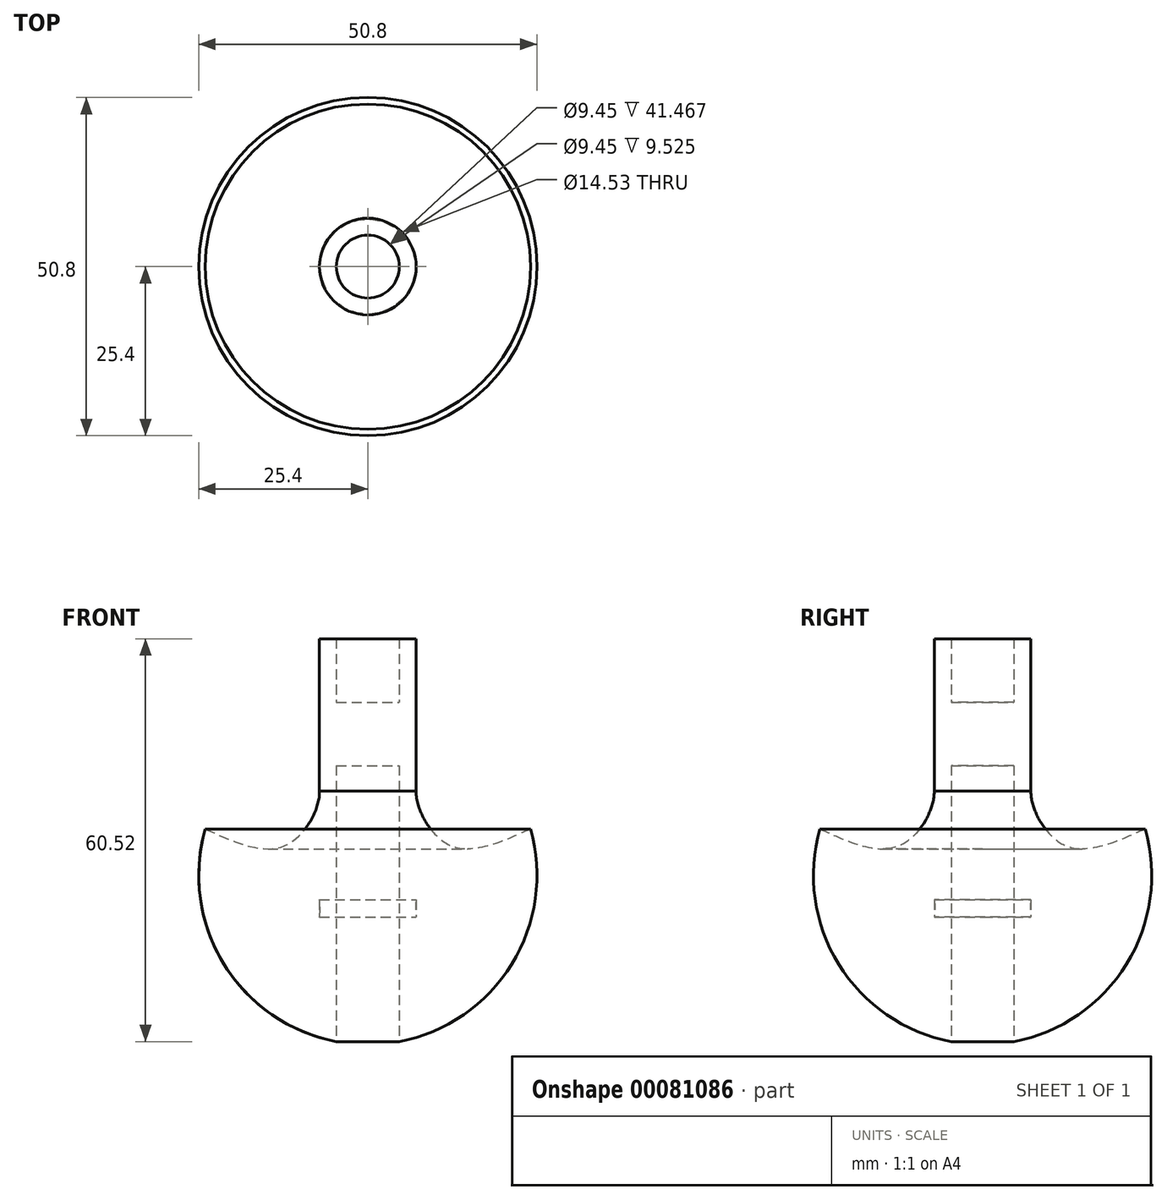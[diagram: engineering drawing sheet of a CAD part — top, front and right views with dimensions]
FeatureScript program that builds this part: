
annotation { "Feature Type Name" : "Feature", "Feature Type Description" : "" }
export const myFeature = defineFeature(function(context is Context, id is Id, definition is map)
    precondition{}
    {
        {
            var Q0;
            Q0=qCreatedBy(makeId("Front.planeOp"),FACE);
            var sketch = newSketch(context, id + "F0", { "sketchPlane" : qUnion([Q0])});
            skArc(sketch, "E0", {"start": v(-22.54, 16.5) * mm, "mid": v(-25.88, -10.52) * mm, "end": v(-4.63, -27.55) * mm});
            skArc(sketch, "E1", {"start": v(-19.3, 16.5) * mm, "mid": v(-23.4, -9.9) * mm, "end": v(-1.6, -25.35) * mm});
            skLineSegment(sketch, "E2", {"start": v(0, 0) * mm, "end": v(0, 16.51) * mm});
            skLineSegment(sketch, "E3", {"start": v(0, 16.51) * mm, "end": v(-7.26, 16.51) * mm});
            skLineSegment(sketch, "E4", {"start": v(-22.54, 16.51) * mm, "end": v(-19.3, 16.51) * mm});
            skLineSegment(sketch, "E5", {"start": v(0, 0) * mm, "end": v(0, -27.94) * mm});
            skLineSegment(sketch, "E6", {"start": v(0, -27.94) * mm, "end": v(0, 35.56) * mm});
            skLineSegment(sketch, "E7", {"start": v(-4.72, 35.56) * mm, "end": v(-4.72, -24.96) * mm});
            skLineSegment(sketch, "E8", {"start": v(-4.72, 35.56) * mm, "end": v(-7.26, 35.56) * mm});
            skLineSegment(sketch, "E9", {"start": v(-7.26, 35.56) * mm, "end": v(-7.26, -24.34) * mm});
            skLineSegment(sketch, "E10", {"start": v(0, 35.56) * mm, "end": v(0, 26.03) * mm});
            skLineSegment(sketch, "E11", {"start": v(0, 26.03) * mm, "end": v(-4.72, 26.03) * mm});
            skLineSegment(sketch, "E12.trimOffspring", {"start": v(-7.26, 16.51) * mm, "end": v(22.54, 16.51) * mm});
            skLineSegment(sketch, "E13.trimOffspring", {"start": v(-19.3, 16.51) * mm, "end": v(-22.54, 16.51) * mm});
            skPoint(sketch, "E14", {"position": v(-15.1, 0) * mm});
            skPoint(sketch, "E15", {"position": v(-7.26, -3.67) * mm});
            skPoint(sketch, "E16", {"position": v(-16.16, -5.93) * mm});
            skPoint(sketch, "E17", {"position": v(-24.25, -7.55) * mm});
            skLineSegment(sketch, "E18", {"start": v(-24.25, -7.55) * mm, "end": v(-24.25, -7.55) * mm});
            skPoint(sketch, "E19", {"position": v(-7.26, 12.37) * mm});
            skPoint(sketch, "E20", {"position": v(-24.43, 6.97) * mm});
            skPoint(sketch, "E21", {"position": v(-12.38, 4.51) * mm});
            skPoint(sketch, "E22.3.internal.snap0", {"position": v(7.64, 16.51) * mm});
            skFitSpline(sketch, "E22", {"points": [v(-24.43, 6.97) * mm, v(-12.38, 4.51) * mm, v(-7.26, 12.37) * mm, v(-9.1, 16.51) * mm], "startDerivative": vector(32.41, -14.69) * mm, "endDerivative": vector(-11.55, 14.27) * mm});
            skArc(sketch, "E23.trimOffspring", {"start": v(-7.26, -6.25) * mm, "mid": v(-7.17, -4.96) * mm, "end": v(-7.26, -3.67) * mm});
            skLineSegment(sketch, "E24", {"start": v(-1.6, -27.8) * mm, "end": v(-13.82, -26.79) * mm});
            skLineSegment(sketch, "E25", {"start": v(0, -27.94) * mm, "end": v(0, -5.84) * mm});
            skLineSegment(sketch, "E26", {"start": v(0, -5.84) * mm, "end": v(-1.6, -5.84) * mm});
            skLineSegment(sketch, "E27", {"start": v(-1.6, -5.84) * mm, "end": v(-1.6, -27.8) * mm});
            skArc(sketch, "E28.trimOffspring", {"start": v(0, -27.94) * mm, "mid": v(24.92, -12.64) * mm, "end": v(22.54, 16.51) * mm});
            skArc(sketch, "E29.trimOffspring", {"start": v(0, -25.4) * mm, "mid": v(23.07, -10.63) * mm, "end": v(19.3, 16.51) * mm});
            skSolve(sketch);
        }
        {
            var Q0;
            {var subQ0=sQuery(id+"F0.wireOp",EDGE,"E18");var subQ1=sQuery(id+"F0.wireOp",EDGE,"E9");var subQ2=makeQuery(id+"F0.imprint","INTERSECT",VERTEX,{"disambiguationData":[OD(0.0)],"derivedFrom":[subQ1,subQ0]});Q0=makeQuery(id+"F0.imprint","IMPRINT",FACE,{"disambiguationData":[TD([[makeQuery(id+"F0.imprint","IMPRINT",EDGE,{"disambiguationData":[TD([[subQ2,-1.0]])],"derivedFrom":subQ1}),1.0]])]});}
            var Q1;
            {var subQ0=sQuery(id+"F0.wireOp",EDGE,"E9");var subQ1=sQuery(id+"F0.wireOp",EDGE,"E1");var subQ2=makeQuery(id+"F0.imprint","INTERSECT",VERTEX,{"derivedFrom":[subQ1,subQ0]});Q1=makeQuery(id+"F0.imprint","IMPRINT",FACE,{"disambiguationData":[TD([[makeQuery(id+"F0.imprint","IMPRINT",EDGE,{"disambiguationData":[TD([[subQ2,1.0]])],"derivedFrom":subQ1}),1.0]])]});}
            var Q2;
            {var subQ0=sQuery(id+"F0.wireOp",EDGE,"E11");Q2=makeQuery(id+"F0.imprint","IMPRINT",FACE,{"disambiguationData":[TD([[makeQuery(id+"F0.imprint","IMPRINT",EDGE,{"derivedFrom":subQ0}),1.0]])]});}
            var Q3;
            {var subQ1=sQuery(id+"F0.wireOp",EDGE,"E8");Q3=makeQuery(id+"F0.imprint","IMPRINT",FACE,{"disambiguationData":[TD([[makeQuery(id+"F0.imprint","IMPRINT",EDGE,{"derivedFrom":subQ1}),1.0]])]});}
            var Q4;
            {var subQ4=sQuery(id+"F0.wireOp",EDGE,"E13.trimOffspring");Q4=makeQuery(id+"F0.imprint","IMPRINT",FACE,{"disambiguationData":[TD([[makeQuery(id+"F0.imprint","IMPRINT",EDGE,{"derivedFrom":subQ4}),1.0]])]});}
            var Q5;
            {var subQ0=sQuery(id+"F0.wireOp",EDGE,"E6");var subQ1=makeQuery(id+"F0.imprint","IMPRINT",VERTEX,{"derivedFrom":subQ0});Q5=makeQuery(id+"F0.imprint","IMPRINT",FACE,{"disambiguationData":[TD([[makeQuery(id+"F0.imprint","IMPRINT",EDGE,{"disambiguationData":[TD([[subQ1,1.0]])],"derivedFrom":subQ0}),1.0]])]});}
            var Q6;
            {var subQ1=sQuery(id+"F0.wireOp",EDGE,"E1");var subQ8=sQuery(id+"F0.wireOp",EDGE,"E7");var subQ9=makeQuery(id+"F0.imprint","INTERSECT",VERTEX,{"derivedFrom":[subQ1,subQ8]});Q6=makeQuery(id+"F0.imprint","IMPRINT",FACE,{"disambiguationData":[TD([[makeQuery(id+"F0.imprint","IMPRINT",EDGE,{"disambiguationData":[TD([[subQ9,1.0]])],"derivedFrom":subQ1}),1.0]])]});}
            var Q7;
            Q7=sQuery(id+"F0.wireOp",EDGE,"E6");
            revolve(context, id + "F1", {"entities" : qUnion([Q0, Q1, Q2, Q3, Q4, Q5, Q6]), "axis" : qUnion([Q7]), "revolveType" : RevolveType.FULL});
        }
    });
